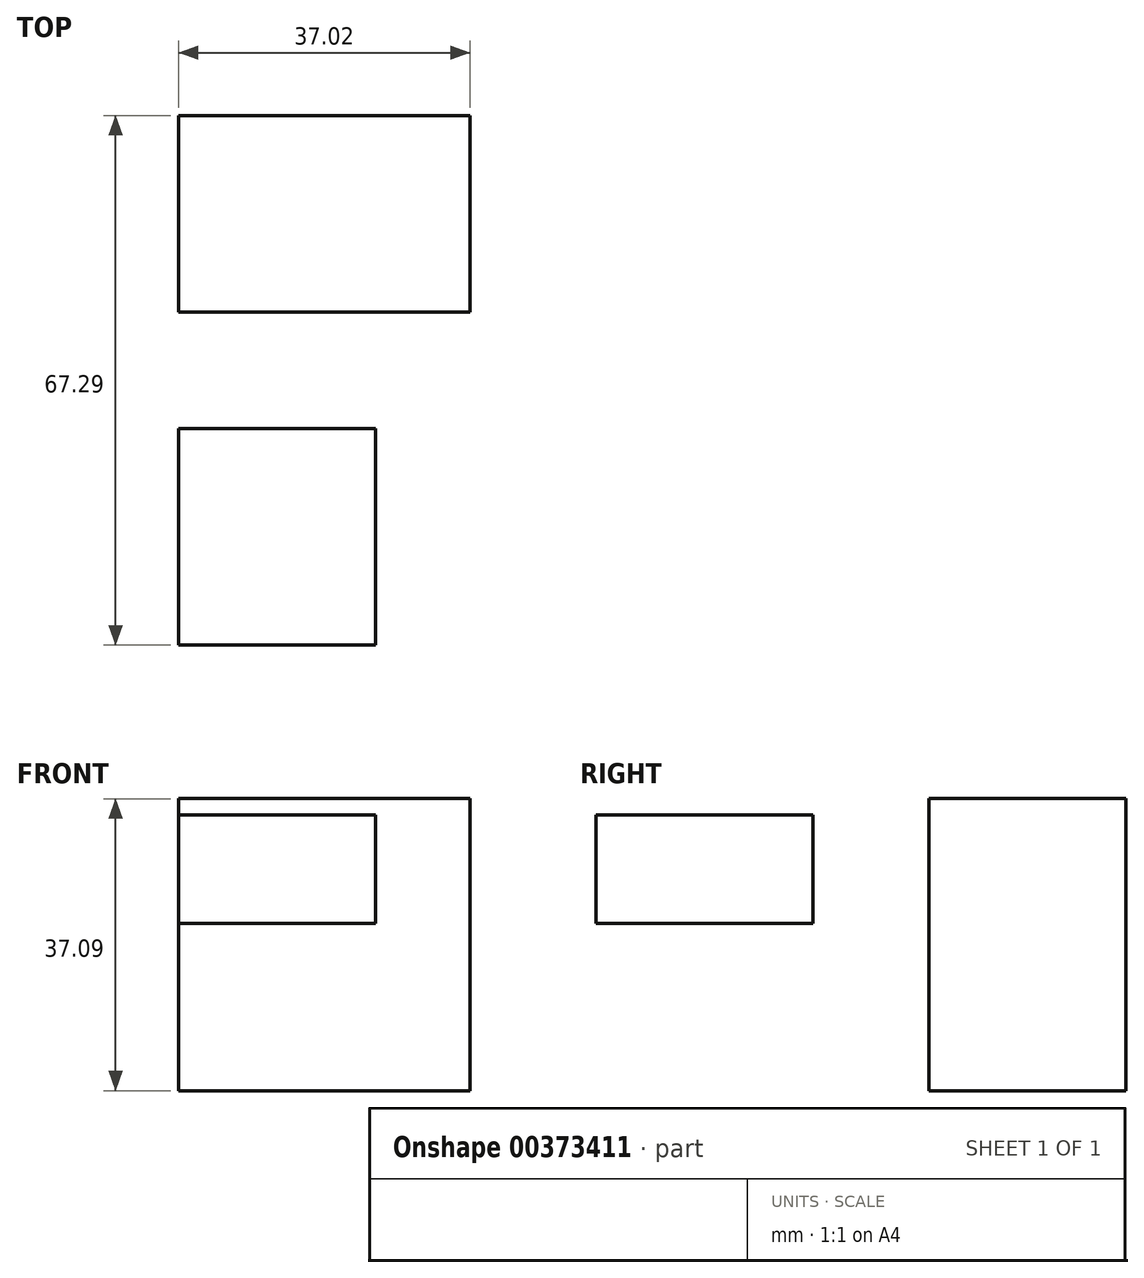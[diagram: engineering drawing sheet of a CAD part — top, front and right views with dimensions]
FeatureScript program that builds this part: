
annotation { "Feature Type Name" : "Feature", "Feature Type Description" : "" }
export const myFeature = defineFeature(function(context is Context, id is Id, definition is map)
    precondition{}
    {
        {
            var Q0;
            Q0=qCreatedBy(makeId("Front.planeOp"),FACE);
            var sketch = newSketch(context, id + "F0", { "sketchPlane" : qUnion([Q0])});
            skLineSegment(sketch, "E0.bottom", {"start": v(37.02, 37.1) * mm, "end": v(0, 37.1) * mm});
            skLineSegment(sketch, "E0.top", {"start": v(37.02, 0) * mm, "end": v(0, 0) * mm});
            skLineSegment(sketch, "E0.left", {"start": v(37.02, 37.1) * mm, "end": v(37.02, 0) * mm});
            skLineSegment(sketch, "E0.right", {"start": v(0, 37.1) * mm, "end": v(0, 0) * mm});
            skPoint(sketch, "E1.firstSnap0", {"position": v(0, 18.55) * mm});
            skPoint(sketch, "E1.oppositeSnap0", {"position": v(0, 18.55) * mm});
            skLineSegment(sketch, "E1.bottom", {"start": v(-13.44, 18.55) * mm, "end": v(21.93, 18.55) * mm});
            skLineSegment(sketch, "E1.top", {"start": v(-13.44, 18.55) * mm, "end": v(21.93, 18.55) * mm});
            skLineSegment(sketch, "E1.left", {"start": v(-13.44, 18.55) * mm, "end": v(-13.44, 18.55) * mm});
            skLineSegment(sketch, "E1.right", {"start": v(21.93, 18.55) * mm, "end": v(21.93, 18.55) * mm});
            skLineSegment(sketch, "E2.bottom", {"start": v(-13.44, 18.55) * mm, "end": v(-5.46, 18.55) * mm});
            skLineSegment(sketch, "E2.top", {"start": v(-13.44, 18.55) * mm, "end": v(-5.46, 18.55) * mm});
            skLineSegment(sketch, "E2.right", {"start": v(-5.46, 18.55) * mm, "end": v(-5.46, 18.55) * mm});
            skSolve(sketch);
        }
        {
            var Q0;
            {var subQ0=sQuery(id+"F0.wireOp",EDGE,"E0.bottom");Q0=makeQuery(id+"F0.imprint","IMPRINT",FACE,{"disambiguationData":[TD([[makeQuery(id+"F0.imprint","IMPRINT",EDGE,{"derivedFrom":subQ0}),1.0]])]});}
            var Q1;
            Q1 = qSketchRegion(id + "FQXM29mvimg3oh4_0", true);
            extrude(context, id + "F1", {"entities" : qUnion([Q0, Q1]), "depth" : 25 * mm});
        }
        {
            var Q0;
            Q0=qCreatedBy(makeId("Right.planeOp"),FACE);
            var sketch = newSketch(context, id + "F2", { "sketchPlane" : qUnion([Q0])});
            skLineSegment(sketch, "E3.bottom", {"start": v(-67.29, 35) * mm, "end": v(-39.75, 35) * mm});
            skLineSegment(sketch, "E3.top", {"start": v(-67.29, 21.23) * mm, "end": v(-39.75, 21.23) * mm});
            skLineSegment(sketch, "E3.left", {"start": v(-67.29, 35) * mm, "end": v(-67.29, 21.23) * mm});
            skLineSegment(sketch, "E3.right", {"start": v(-39.75, 35) * mm, "end": v(-39.75, 21.23) * mm});
            skSolve(sketch);
        }
        {
            var Q0;
            Q0 = qSketchRegion(id + "F2", true);
            extrude(context, id + "F3", {"entities" : qUnion([Q0]), "depth" : 25 * mm});
        }
    });
